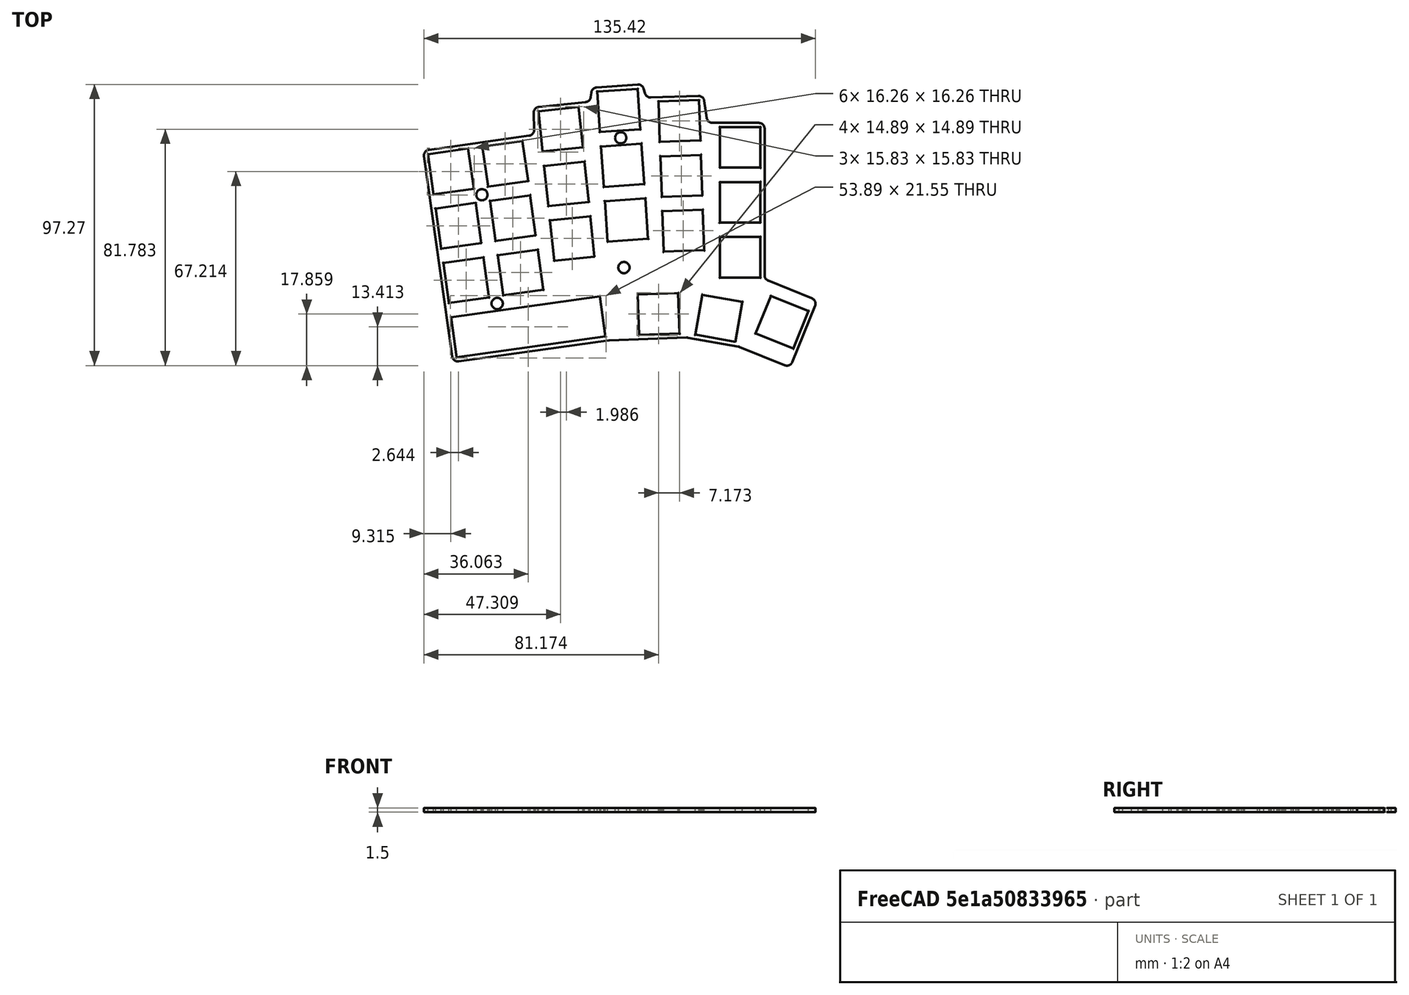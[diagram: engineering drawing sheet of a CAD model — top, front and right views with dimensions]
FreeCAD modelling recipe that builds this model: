
FCSTD DOCUMENT  (FreeCAD 0.21R)
Label: plate
License: All rights reserved
LicenseURL: http://en.wikipedia.org/wiki/All_rights_reserved
objects: Sketcher::SketchObject×2, PartDesign::Pad×1, PartDesign::Hole×1, PartDesign::Fillet×1, PartDesign::Body×1
note: 9 computed .brp shape members not serialized (recipe doc carries the construction recipe); baked Part::Feature solids carry a one-line shape summary decoded from their .brp

FEATURE [Sketcher::SketchObject] Sketch
  FullyConstrained = false
  sketch-geometry (122):
    g0: LineSegment StartX=-61.3939 StartY=-28.7221 StartZ=0 EndX=-47.5301 EndY=-26.7737 EndZ=0
    g1: LineSegment StartX=-47.5301 StartY=-26.7737 StartZ=0 EndX=-49.4786 EndY=-12.9099 EndZ=0
    g2: LineSegment StartX=-49.4786 StartY=-12.9099 StartZ=0 EndX=-63.3423 EndY=-14.8583 EndZ=0
    g3: LineSegment StartX=-63.3423 StartY=-14.8583 StartZ=0 EndX=-61.3939 EndY=-28.7221 EndZ=0
    g4: LineSegment StartX=-64.0382 StartY=-9.90699 StartZ=0 EndX=-50.1744 EndY=-7.95857 EndZ=0
    g5: LineSegment StartX=-50.1744 StartY=-7.95857 StartZ=0 EndX=-52.1228 EndY=5.90518 EndZ=0
    g6: LineSegment StartX=-52.1228 StartY=5.90518 StartZ=0 EndX=-65.9866 EndY=3.95676 EndZ=0
    g7: LineSegment StartX=-65.9866 StartY=3.95676 StartZ=0 EndX=-64.0382 EndY=-9.90699 EndZ=0
    g8: LineSegment StartX=-66.6825 StartY=8.9081 StartZ=0 EndX=-52.8187 EndY=10.8565 EndZ=0
    g9: LineSegment StartX=-54.7671 StartY=24.7203 StartZ=0 EndX=-68.6309 EndY=22.7719 EndZ=0
    g10: LineSegment StartX=-68.6309 StartY=22.7719 StartZ=0 EndX=-66.6825 EndY=8.9081 EndZ=0
    g11: LineSegment StartX=-42.5788 StartY=-26.0778 StartZ=0 EndX=-28.715 EndY=-24.1294 EndZ=0
    g12: LineSegment StartX=-28.715 StartY=-24.1294 StartZ=0 EndX=-30.6635 EndY=-10.2656 EndZ=0
    g13: LineSegment StartX=-30.6635 StartY=-10.2656 StartZ=0 EndX=-44.5272 EndY=-12.214 EndZ=0
    g14: LineSegment StartX=-44.5272 StartY=-12.214 StartZ=0 EndX=-42.5788 EndY=-26.0778 EndZ=0
    g15: LineSegment StartX=-45.2231 StartY=-7.2627 StartZ=0 EndX=-31.3593 EndY=-5.31428 EndZ=0
    g16: LineSegment StartX=-31.3593 StartY=-5.31428 StartZ=0 EndX=-33.3077 EndY=8.54947 EndZ=0
    g17: LineSegment StartX=-33.3077 StartY=8.54947 StartZ=0 EndX=-47.1715 EndY=6.60105 EndZ=0
    g18: LineSegment StartX=-47.1715 StartY=6.60105 StartZ=0 EndX=-45.2231 EndY=-7.2627 EndZ=0
    g19: LineSegment StartX=-47.8674 StartY=11.5524 StartZ=0 EndX=-34.0036 EndY=13.5008 EndZ=0
    g20: LineSegment StartX=-34.0036 StartY=13.5008 StartZ=0 EndX=-35.952 EndY=27.3646 EndZ=0
    g21: LineSegment StartX=-35.952 StartY=27.3646 StartZ=0 EndX=-49.8158 EndY=25.4161 EndZ=0
    g22: LineSegment StartX=-49.8158 StartY=25.4161 StartZ=0 EndX=-47.8674 EndY=11.5524 EndZ=0
    g23: LineSegment StartX=-24.9886 StartY=-14.1019 StartZ=0 EndX=-11.0653 EndY=-12.6385 EndZ=0
    g24: LineSegment StartX=-11.0653 StartY=-12.6385 StartZ=0 EndX=-12.5287 EndY=1.28477 EndZ=0
    g25: LineSegment StartX=-12.5287 StartY=1.28477 StartZ=0 EndX=-26.452 EndY=-0.178632 EndZ=0
    g26: LineSegment StartX=-26.452 StartY=-0.178632 StartZ=0 EndX=-24.9886 EndY=-14.1019 EndZ=0
    g27: LineSegment StartX=-26.9746 StartY=4.79398 StartZ=0 EndX=-13.0513 EndY=6.25738 EndZ=0
    g28: LineSegment StartX=-13.0513 StartY=6.25738 StartZ=0 EndX=-14.5147 EndY=20.1807 EndZ=0
    g29: LineSegment StartX=-14.5147 StartY=20.1807 StartZ=0 EndX=-28.438 EndY=18.7173 EndZ=0
    g30: LineSegment StartX=-28.438 StartY=18.7173 StartZ=0 EndX=-26.9746 EndY=4.79398 EndZ=0
    g31: LineSegment StartX=-28.9607 StartY=23.6899 StartZ=0 EndX=-15.0374 EndY=25.1533 EndZ=0
    g32: LineSegment StartX=-15.0374 StartY=25.1533 StartZ=0 EndX=-16.5008 EndY=39.0766 EndZ=0
    g33: LineSegment StartX=-16.5008 StartY=39.0766 StartZ=0 EndX=-30.4241 EndY=37.6132 EndZ=0
    g34: LineSegment StartX=-30.4241 StartY=37.6132 StartZ=0 EndX=-28.9607 EndY=23.6899 EndZ=0
    g35: LineSegment StartX=-6.49465 StartY=-7.47124 StartZ=0 EndX=7.47124 EndY=-6.49465 EndZ=0
    g36: LineSegment StartX=7.47124 StartY=-6.49465 StartZ=0 EndX=6.49465 EndY=7.47124 EndZ=0
    g37: LineSegment StartX=6.49465 StartY=7.47124 StartZ=0 EndX=-7.47124 EndY=6.49465 EndZ=0
    g38: LineSegment StartX=-7.47124 StartY=6.49465 StartZ=0 EndX=-6.49465 EndY=-7.47124 EndZ=0
    g39: LineSegment StartX=-7.82003 StartY=11.4825 StartZ=0 EndX=6.14587 EndY=12.4591 EndZ=0
    g40: LineSegment StartX=6.14587 StartY=12.4591 StartZ=0 EndX=5.16928 EndY=26.425 EndZ=0
    g41: LineSegment StartX=5.16928 StartY=26.425 StartZ=0 EndX=-8.79662 EndY=25.4484 EndZ=0
    g42: LineSegment StartX=-8.79662 StartY=25.4484 StartZ=0 EndX=-7.82003 EndY=11.4825 EndZ=0
    g43: LineSegment StartX=-9.1454 StartY=30.4362 StartZ=0 EndX=4.8205 EndY=31.4128 EndZ=0
    g44: LineSegment StartX=4.8205 StartY=31.4128 StartZ=0 EndX=3.84391 EndY=45.3787 EndZ=0
    g45: LineSegment StartX=3.84391 StartY=45.3787 StartZ=0 EndX=-10.122 EndY=44.4021 EndZ=0
    g46: LineSegment StartX=-10.122 StartY=44.4021 StartZ=0 EndX=-9.1454 EndY=30.4362 EndZ=0
    g47: LineSegment StartX=12.8821 StartY=-10.9669 StartZ=0 EndX=26.8736 EndY=-10.4783 EndZ=0
    g48: LineSegment StartX=26.8736 StartY=-10.4783 StartZ=0 EndX=26.385 EndY=3.51319 EndZ=0
    g49: LineSegment StartX=26.385 StartY=3.51319 StartZ=0 EndX=12.3935 EndY=3.0246 EndZ=0
    g50: LineSegment StartX=12.3935 StartY=3.0246 StartZ=0 EndX=12.8821 EndY=-10.9669 EndZ=0
    g51: LineSegment StartX=12.219 StartY=8.02155 StartZ=0 EndX=26.2105 EndY=8.51014 EndZ=0
    g52: LineSegment StartX=26.2105 StartY=8.51014 StartZ=0 EndX=25.7219 EndY=22.5016 EndZ=0
    g53: LineSegment StartX=25.7219 StartY=22.5016 StartZ=0 EndX=11.7304 EndY=22.013 EndZ=0
    g54: LineSegment StartX=11.7304 StartY=22.013 StartZ=0 EndX=12.219 EndY=8.02155 EndZ=0
    g55: LineSegment StartX=11.5559 StartY=27.01 StartZ=0 EndX=25.5474 EndY=27.4986 EndZ=0
    g56: LineSegment StartX=25.5474 StartY=27.4986 StartZ=0 EndX=25.0588 EndY=41.49 EndZ=0
    g57: LineSegment StartX=25.0588 StartY=41.49 StartZ=0 EndX=11.0673 EndY=41.0014 EndZ=0
    g58: LineSegment StartX=11.0673 StartY=41.0014 StartZ=0 EndX=11.5559 EndY=27.01 EndZ=0
    g59: LineSegment StartX=32.2909 StartY=-19.8837 StartZ=0 EndX=46.2909 EndY=-19.8837 EndZ=0
    g60: LineSegment StartX=46.2909 StartY=-19.8837 StartZ=0 EndX=46.2909 EndY=-5.88372 EndZ=0
    g61: LineSegment StartX=46.2909 StartY=-5.88372 StartZ=0 EndX=32.2909 EndY=-5.88372 EndZ=0
    g62: LineSegment StartX=32.2909 StartY=-5.88372 StartZ=0 EndX=32.2909 EndY=-19.8837 EndZ=0
    g63: LineSegment StartX=32.2909 StartY=-0.883724 StartZ=0 EndX=46.2909 EndY=-0.883724 EndZ=0
    g64: LineSegment StartX=46.2909 StartY=-0.883724 StartZ=0 EndX=46.2909 EndY=13.1163 EndZ=0
    g65: LineSegment StartX=46.2909 StartY=13.1163 StartZ=0 EndX=32.2909 EndY=13.1163 EndZ=0
    g66: LineSegment StartX=32.2909 StartY=13.1163 StartZ=0 EndX=32.2909 EndY=-0.883724 EndZ=0
    g67: LineSegment StartX=32.2909 StartY=18.1163 StartZ=0 EndX=46.2909 EndY=18.1163 EndZ=0
    g68: LineSegment StartX=46.2909 StartY=18.1163 StartZ=0 EndX=46.2909 EndY=32.1163 EndZ=0
    g69: LineSegment StartX=46.2909 StartY=32.1163 StartZ=0 EndX=32.2909 EndY=32.1163 EndZ=0
    g70: LineSegment StartX=32.2909 StartY=32.1163 StartZ=0 EndX=32.2909 EndY=18.1163 EndZ=0
    g71: LineSegment StartX=-60.698 StartY=-33.6734 StartZ=0 EndX=-58.7496 EndY=-47.5372 EndZ=0
    g72: LineSegment StartX=-7.25565 StartY=-40.3002 StartZ=0 EndX=-9.20408 EndY=-26.4364 EndZ=0
    g73: LineSegment StartX=4.38254 StartY=-39.7811 StartZ=0 EndX=18.374 EndY=-39.2925 EndZ=0
    g74: LineSegment StartX=18.374 StartY=-39.2925 StartZ=0 EndX=17.8854 EndY=-25.301 EndZ=0
    g75: LineSegment StartX=17.8854 StartY=-25.301 StartZ=0 EndX=3.89395 EndY=-25.7896 EndZ=0
    g76: LineSegment StartX=3.89395 StartY=-25.7896 StartZ=0 EndX=4.38254 EndY=-39.7811 EndZ=0
    g77: LineSegment StartX=23.8559 StartY=-39.6758 StartZ=0 EndX=37.6432 EndY=-42.1069 EndZ=0
    g78: LineSegment StartX=37.6432 StartY=-42.1069 StartZ=0 EndX=40.0743 EndY=-28.3196 EndZ=0
    g79: LineSegment StartX=40.0743 StartY=-28.3196 StartZ=0 EndX=26.287 EndY=-25.8885 EndZ=0
    g80: LineSegment StartX=26.287 StartY=-25.8885 StartZ=0 EndX=23.8559 EndY=-39.6758 EndZ=0
    g81: LineSegment StartX=44.7049 StartY=-39.2174 StartZ=0 EndX=57.6855 EndY=-44.4619 EndZ=0
    g82: LineSegment StartX=57.6855 StartY=-44.4619 StartZ=0 EndX=62.93 EndY=-31.4814 EndZ=0
    g83: LineSegment StartX=62.93 StartY=-31.4814 StartZ=0 EndX=49.9494 EndY=-26.2369 EndZ=0
    g84: LineSegment StartX=49.9494 StartY=-26.2369 StartZ=0 EndX=44.7049 EndY=-39.2174 EndZ=0
    g85: LineSegment StartX=-54.7671 StartY=24.7203 StartZ=0 EndX=-52.8187 EndY=10.8565 EndZ=0
    g86: LineSegment StartX=-60.698 StartY=-33.6734 StartZ=0 EndX=-9.20408 EndY=-26.4364 EndZ=0
    g87: LineSegment StartX=-58.7496 StartY=-47.5372 StartZ=0 EndX=-7.25565 EndY=-40.3002 EndZ=0
    g88: ArcOfCircle CenterX=4.0455 CenterY=44.8665 CenterZ=0 NormalX=0 NormalY=0 NormalZ=1 AngleXU=0 Radius=2 StartAngle=0.28778 EndAngle=1.64061
    g89: ArcOfCircle CenterX=29.748 CenterY=35.5913 CenterZ=0 NormalX=0 NormalY=0 NormalZ=1 AngleXU=0 Radius=2 StartAngle=3.287 EndAngle=4.71239
    g90: LineSegment StartX=26.898 StartY=41.2496 StartZ=0 EndX=27.7691 EndY=35.3015 EndZ=0
    g91: ArcOfCircle CenterX=24.9191 CenterY=40.9598 CenterZ=0 NormalX=0 NormalY=0 NormalZ=1 AngleXU=0 Radius=2 StartAngle=0.145412 EndAngle=1.6057
    g92: LineSegment StartX=8.42966 StartY=42.3852 StartZ=0 EndX=24.8493 EndY=42.9586 EndZ=0
    g93: LineSegment StartX=5.96326 StartY=45.4341 StartZ=0 EndX=6.44211 EndY=43.8164 EndZ=0
    g94: ArcOfCircle CenterX=8.35986 CenterY=44.384 CenterZ=0 NormalX=0 NormalY=0 NormalZ=1 AngleXU=0 Radius=2 StartAngle=3.42937 EndAngle=4.7473
    g95: LineSegment StartX=-10.2931 StartY=45.8687 StartZ=0 EndX=3.90599 EndY=46.8616 EndZ=0
    g96: ArcOfCircle CenterX=-10.1536 CenterY=43.8736 CenterZ=0 NormalX=0 NormalY=0 NormalZ=1 AngleXU=0 Radius=2 StartAngle=1.64061 EndAngle=3.0267
    g97: LineSegment StartX=-12.317 StartY=42.5724 StartZ=0 EndX=-12.1404 EndY=44.1029 EndZ=0
    g98: ArcOfCircle CenterX=-14.3038 CenterY=42.8016 CenterZ=0 NormalX=0 NormalY=0 NormalZ=1 AngleXU=0 Radius=2 StartAngle=4.81711 EndAngle=6.16829
    g99: ArcOfCircle CenterX=-33.9327 CenterY=31.1575 CenterZ=0 NormalX=0 NormalY=0 NormalZ=1 AngleXU=0 Radius=2 StartAngle=4.85202 EndAngle=6.31188
    g100: LineSegment StartX=-31.9335 StartY=31.2149 StartZ=0 EndX=-32.1013 EndY=37.0618 EndZ=0
    g101: LineSegment StartX=-30.3112 StartY=39.1082 StartZ=0 EndX=-14.0947 EndY=40.8126 EndZ=0
    g102: ArcOfCircle CenterX=-30.1021 CenterY=37.1191 CenterZ=0 NormalX=0 NormalY=0 NormalZ=1 AngleXU=0 Radius=2 StartAngle=1.67552 EndAngle=3.17029
    g103: LineSegment StartX=-68.3163 StartY=24.3056 StartZ=0 EndX=-33.6543 EndY=29.177 EndZ=0
    g104: ArcOfCircle CenterX=-68.0379 CenterY=22.325 CenterZ=0 NormalX=0 NormalY=0 NormalZ=1 AngleXU=0 Radius=2 StartAngle=1.71042 EndAngle=3.28122
    g105: LineSegment StartX=-60.2833 StartY=-47.2226 StartZ=0 EndX=-70.0185 EndY=22.0467 EndZ=0
    g106: ArcOfCircle CenterX=-58.3028 CenterY=-46.9442 CenterZ=0 NormalX=0 NormalY=0 NormalZ=1 AngleXU=0 Radius=2 StartAngle=3.28122 EndAngle=4.85202
    g107: LineSegment StartX=-6.16364 StartY=-41.6362 StartZ=0 EndX=-58.0244 EndY=-48.9248 EndZ=0
    g108: ArcOfCircle CenterX=-5.8853 CenterY=-43.6167 CenterZ=0 NormalX=0 NormalY=0 NormalZ=1 AngleXU=0 Radius=2 StartAngle=1.6057 EndAngle=1.71042
    g109: LineSegment StartX=-5.9551 StartY=-41.618 StartZ=0 EndX=20.8216 EndY=-40.6829 EndZ=0
    g110: ArcOfCircle CenterX=20.8913 CenterY=-42.6817 CenterZ=0 NormalX=0 NormalY=0 NormalZ=1 AngleXU=0 Radius=2 StartAngle=1.39626 EndAngle=1.6057
    g111: LineSegment StartX=21.2386 StartY=-40.7121 StartZ=0 EndX=38.6232 EndY=-43.7774 EndZ=0
    g112: ArcOfCircle CenterX=38.2759 CenterY=-45.747 CenterZ=0 NormalX=0 NormalY=0 NormalZ=1 AngleXU=0 Radius=2 StartAngle=1.18682 EndAngle=1.39626
    g113: LineSegment StartX=54.7778 StartY=-50.2572 StartZ=0 EndX=39.0251 EndY=-43.8927 EndZ=0
    g114: ArcOfCircle CenterX=55.5271 CenterY=-48.4028 CenterZ=0 NormalX=0 NormalY=0 NormalZ=1 AngleXU=0 Radius=2 StartAngle=4.32842 EndAngle=5.89921
    g115: LineSegment StartX=29.748 StartY=33.5913 StartZ=0 EndX=45.7909 EndY=33.5913 EndZ=0
    g116: ArcOfCircle CenterX=45.7909 CenterY=31.5913 CenterZ=0 NormalX=0 NormalY=0 NormalZ=1 AngleXU=0 Radius=2 StartAngle=0 EndAngle=1.5708
    g117: LineSegment StartX=65.2341 StartY=-29.7159 StartZ=0 EndX=57.3814 EndY=-49.152 EndZ=0
    g118: ArcOfCircle CenterX=63.3798 CenterY=-28.9667 CenterZ=0 NormalX=0 NormalY=0 NormalZ=1 AngleXU=0 Radius=2 StartAngle=5.89921 EndAngle=7.47001
    g119: LineSegment StartX=64.129 StartY=-27.1124 StartZ=0 EndX=49.0416 EndY=-21.0167 EndZ=0
    g120: LineSegment StartX=47.7909 StartY=-19.1623 StartZ=0 EndX=47.7909 EndY=31.5913 EndZ=0
    g121: ArcOfCircle CenterX=49.7909 CenterY=-19.1623 CenterZ=0 NormalX=0 NormalY=0 NormalZ=1 AngleXU=0 Radius=2 StartAngle=3.14159 EndAngle=4.32842
  constraints (122):
    c: Coincident(g104,g105)
    c: Coincident(g9,g10)
    c: Coincident(g103,g104)
    c: Coincident(g8,g10)
    c: Coincident(g6,g7)
    c: Coincident(g4,g7)
    c: Coincident(g2,g3)
    c: Coincident(g0,g3)
    c: Coincident(g71,g86)
    c: Coincident(g105,g106)
    c: Coincident(g71,g87)
    c: Coincident(g106,g107)
    c: Coincident(g9,g85)
    c: Coincident(g8,g85)
    c: Coincident(g5,g6)
    c: Coincident(g4,g5)
    c: Coincident(g21,g22)
    c: Coincident(g1,g2)
    c: Coincident(g19,g22)
    c: Coincident(g0,g1)
    c: Coincident(g17,g18)
    c: Coincident(g15,g18)
    c: Coincident(g13,g14)
    c: Coincident(g11,g14)
    c: Coincident(g20,g21)
    c: Coincident(g19,g20)
    c: Coincident(g99,g103)
    c: Coincident(g16,g17)
    c: Coincident(g100,g102)
    c: Coincident(g99,g100)
    c: Coincident(g15,g16)
    c: Coincident(g12,g13)
    c: Coincident(g33,g34)
    c: Coincident(g101,g102)
    c: Coincident(g31,g34)
    c: Coincident(g11,g12)
    c: Coincident(g29,g30)
    c: Coincident(g27,g30)
    c: Coincident(g25,g26)
    c: Coincident(g23,g26)
    c: Coincident(g32,g33)
    c: Coincident(g31,g32)
    c: Coincident(g28,g29)
    c: Coincident(g98,g101)
    c: Coincident(g27,g28)
    c: Coincident(g24,g25)
    c: Coincident(g97,g98)
    c: Coincident(g96,g97)
    c: Coincident(g23,g24)
    c: Coincident(g95,g96)
    c: Coincident(g45,g46)
    c: Coincident(g43,g46)
    c: Coincident(g41,g42)
    c: Coincident(g39,g42)
    c: Coincident(g37,g38)
    c: Coincident(g35,g38)
    c: Coincident(g107,g108)
    c: Coincident(g108,g109)
    c: Coincident(g44,g45)
    c: Coincident(g75,g76)
    c: Coincident(g88,g95)
    c: Coincident(g73,g76)
    c: Coincident(g43,g44)
    c: Coincident(g40,g41)
    c: Coincident(g88,g93)
    c: Coincident(g39,g40)
    c: Coincident(g93,g94)
    c: Coincident(g36,g37)
    c: Coincident(g35,g36)
    c: Coincident(g92,g94)
    c: Coincident(g57,g58)
    c: Coincident(g55,g58)
    c: Coincident(g53,g54)
    c: Coincident(g51,g54)
    c: Coincident(g49,g50)
    c: Coincident(g47,g50)
    c: Coincident(g74,g75)
    c: Coincident(g73,g74)
    c: Coincident(g109,g110)
    c: Coincident(g110,g111)
    c: Coincident(g77,g80)
    c: Coincident(g91,g92)
    c: Coincident(g56,g57)
    c: Coincident(g55,g56)
    c: Coincident(g52,g53)
    c: Coincident(g51,g52)
    c: Coincident(g79,g80)
    c: Coincident(g48,g49)
    c: Coincident(g47,g48)
    c: Coincident(g90,g91)
    c: Coincident(g89,g90)
    c: Coincident(g89,g115)
    c: Coincident(g59,g62)
    c: Coincident(g61,g62)
    c: Coincident(g63,g66)
    c: Coincident(g65,g66)
    c: Coincident(g67,g70)
    c: Coincident(g69,g70)
    c: Coincident(g77,g78)
    c: Coincident(g111,g112)
    c: Coincident(g112,g113)
    c: Coincident(g78,g79)
    c: Coincident(g81,g84)
    c: Coincident(g115,g116)
    c: Coincident(g59,g60)
    c: Coincident(g60,g61)
    c: Coincident(g63,g64)
    c: Coincident(g64,g65)
    c: Coincident(g67,g68)
    c: Coincident(g68,g69)
    c: Coincident(g120,g121)
    c: Coincident(g116,g120)
    c: Coincident(g119,g121)
    c: Coincident(g83,g84)
    c: Coincident(g113,g114)
    c: Coincident(g114,g117)
    c: Coincident(g81,g82)
    c: Coincident(g82,g83)
    c: Coincident(g118,g119)
    c: Coincident(g117,g118)
    c: Coincident(g72,g86)
    c: Coincident(g72,g87)
FEATURE [PartDesign::Pad] Pad
  Direction = (0,0,1)
  Length = 1.5
  Length2 = 10
  Profile = -> Sketch
  ReferenceAxis = -> Sketch [N_Axis]
  Type = 0
FEATURE [Sketcher::SketchObject] Sketch001
  FullyConstrained = false
  MapMode = 5
  Placement = pos=(0,0,1.5) rot=(0,0,1;0rad)
  Support = -> [Pad]
  sketch-geometry (4):
    g0: Circle CenterX=-44.7065 CenterY=-28.9014 CenterZ=0 NormalX=0 NormalY=0 NormalZ=-1 AngleXU=0 Radius=1.1
    g1: Circle CenterX=-49.9951 CenterY=8.72879 CenterZ=0 NormalX=0 NormalY=0 NormalZ=-1 AngleXU=0 Radius=1.1
    g2: Circle CenterX=-1.98806 CenterY=28.4306 CenterZ=0 NormalX=0 NormalY=0 NormalZ=-1 AngleXU=0 Radius=1.1
    g3: Circle CenterX=-0.866417 CenterY=-16.4655 CenterZ=0 NormalX=0 NormalY=0 NormalZ=-1 AngleXU=0 Radius=1.1
FEATURE [PartDesign::Hole] Hole
  BaseFeature = -> Pad
  CustomThreadClearance = 0
  Depth = 336.781
  DepthType = 1
  Diameter = 3.9
  DrillForDepth = false
  DrillPoint = 1
  DrillPointAngle = 118
  HoleCutCountersinkAngle = 90
  HoleCutCustomValues = false
  HoleCutDepth = 0
  HoleCutDiameter = 6.1
  HoleCutType = 0
  ModelThread = false
  Profile = -> Sketch001
  Tapered = false
  TaperedAngle = 90
  ThreadClass = 0
  ThreadDepth = 336.781
  ThreadDepthType = 0
  ThreadDirection = 0
  ThreadFit = 0
  ThreadSize = 10
  ThreadType = 1
  Threaded = false
  UseCustomThreadClearance = false
FEATURE [PartDesign::Fillet] Fillet
  Base = -> Hole [Face5,Face4]
  BaseFeature = -> Hole
  Radius = 0.2
  SupportTransform = false
  UseAllEdges = false
FEATURE [PartDesign::Body] Body
  Group = -> [Sketch,Pad,Sketch001,Hole,Fillet]
  Origin = -> Origin
  Tip = -> Fillet
